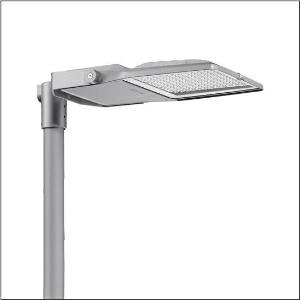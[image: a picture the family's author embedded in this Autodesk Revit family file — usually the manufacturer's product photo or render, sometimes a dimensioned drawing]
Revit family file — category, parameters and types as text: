
# Revit family: floodlight_fl_21_iq_midi___pl61_5xa7781f2c3a_20a4
name_source: partatom
category: Lighting Fixtures
units: mm (PartAtom-declared; Revit-internal decimal feet)

## family parameters
Cut with Voids When Loaded = No
Host = Face
Light Source = No
Part Type = Normal
Room Calculation Point = No
Round Connector Dimension = Use Diameter
Shared = No

## types (1)
- --- (1 x LED, 35100 lm, 270.2 W, 3000K)
    Apparent Load = 270 VA
    CIE Flux Codes = 33 65 98 100 100
    Color Rendering = 70
    Color Temperature = 3000K
    Default Elevation = 1800 mm
    Description = Floodlight FL 21 iQ midi, floodlight, primary light control with lens, of PMMA, primary optical cover: protective disc, of toughened safety glass, transparent, light distribution: PL61, light emission: direct distribution, installation type: surface-mounted, LED, High Power LED, rated luminous flux: 35.100lm, luminous efficacy: 130lm/W, light colour: 730, colour temperature: 3000K, control gear: ECG iQ, control: optimised constant luminous flux control (CLO 2.0), Desk-Remote (wireless, voltage-free reading and setting of iQ features in the workshop via application-optimized NFC function/RFID function), Light-Fading, Smart-Wire, Night-Set, Lumen-Switch, Temp-Guard, Auto-Match, with terminal, 6-pole, mains connection: 220..240V, AC, 50/60Hz, start of lifetime: 270W, end of service life: 287W, reduction: 117W, luminaire housing, of diecast aluminium, powder-coated, Siteco® metallic grey (DB 702S), corrosivity category C5 mid according to DIN EN ISO 12944, sealing non-destructively replaceable, please order mast flange separately, mast bracket, of steel, galvanised, powder-coated, Siteco® metallic grey (DB 702S), protection rating (complete): IP66, insulation class (complete): insulation class II (safety insulation), certification: CE, protection symbol: D, impact resistance: IK08, permissible operating ambient temperature: -40..+40°C, permissible operating ambient temperature for outdoor applications: -40..+50°C, standard: DIN EN 12944, LABS conformity tested according to VDMA 24364:2018-05, packaging unit: 1 piece

Light Distribution: PL61
    Height = 76 mm
    Lamp = 1 x LED
    Lamp Light Flux = 35100 lm
    Lamp Power = 270.2 W
    Lamp count = 1
    Length = 657 mm
    Luminous efficacy = 130 lm/W
    Manufacturer = Siteco
    ModVariant = No
    Model = 5XA7781F2C3A
    Number of Poles = 1
    OnlyDefault = Yes
    Power Factor = 1
    Product Name = Floodlight FL 21 iQ midi | PL61
    Product group = floodlight | pylon annexe
    ProductGroupID = 6200
    Protection Class = Protection class II
    Protection Degree = IP 66
    RLX_Detail_Level = 1
    RLX_Emergency_Light_Flux = 0 lm
    RLX_Emergency_Type = 0
    RLX_Emergency_Type_DB = No
    RlxData = <blob elided: 153621 chars, md5=13b78a75>
    Socket = socket
    Standby Power = 0 W
    System Light Flux = 35100 lm
    System Power = 270 W
    Type Comments = factory setting: luminous flux: 100 % | dim-lin: 254 | 620 mA
    Type Image = l_1007123.jpg
    URL = http://relux.com
    VarID = @adj_038615
    Voltage = 0 V
    Weight = 0.00 kg
    Width = 442 mm

## geometry (parser evidence)
native form markers: Blend x4, Sweep x15
no freeform markers — native parametric forms only
